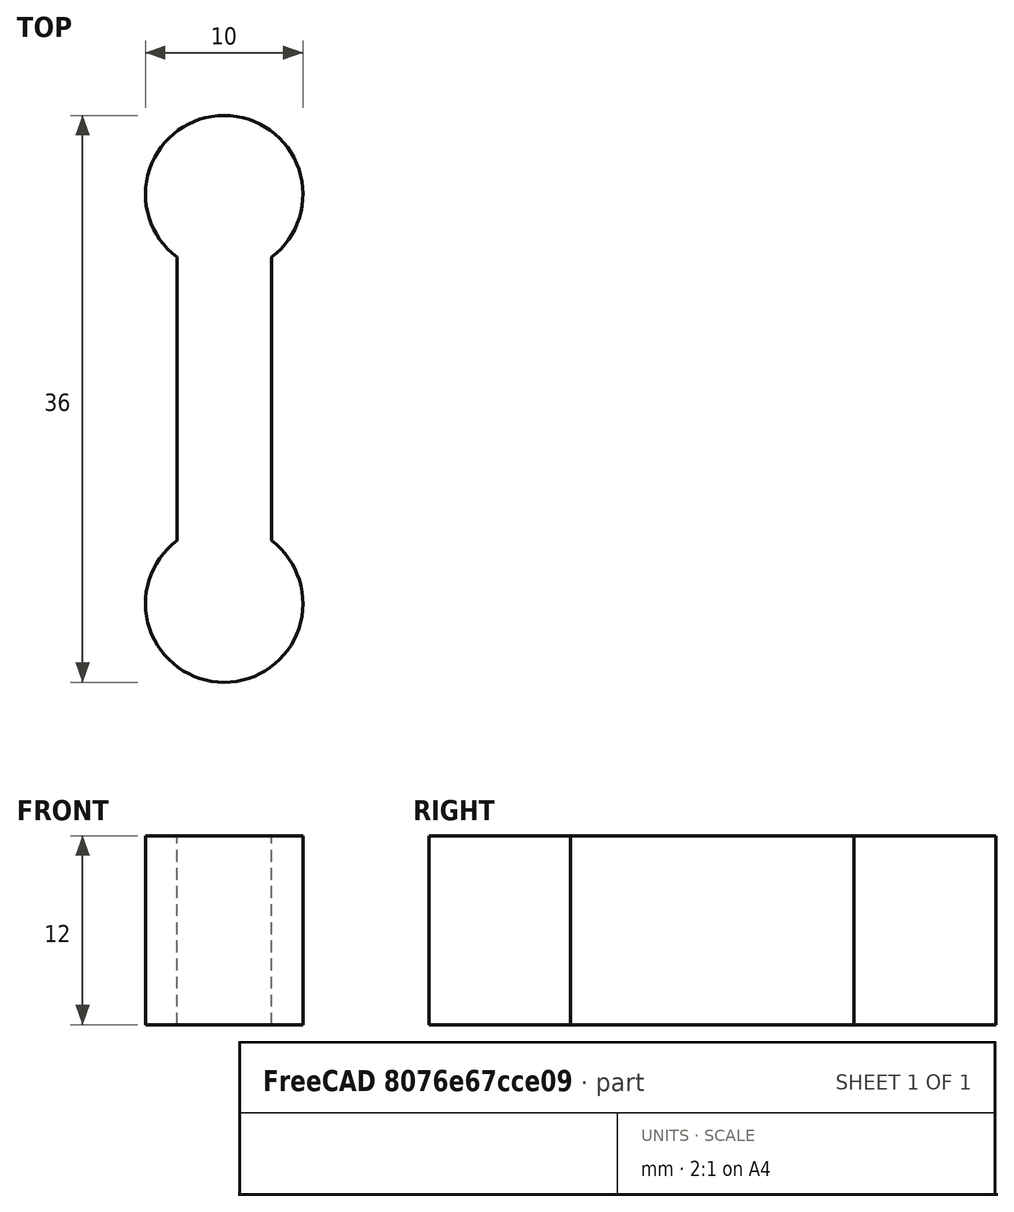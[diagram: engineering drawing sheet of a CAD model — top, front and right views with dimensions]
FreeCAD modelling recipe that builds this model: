
FCSTD DOCUMENT  (FreeCAD 0.19R24291 (Git))
Label: dog bone mk2
License: All rights reserved
LicenseURL: http://en.wikipedia.org/wiki/All_rights_reserved
objects: Sketcher::SketchObject×1, PartDesign::Pad×1, PartDesign::Body×1
note: 4 computed .brp shape members not serialized (recipe doc carries the construction recipe); baked Part::Feature solids carry a one-line shape summary decoded from their .brp

FEATURE [Sketcher::SketchObject] Sketch
  FullyConstrained = true
  MapMode = 5
  Support = -> [XY_Plane]
  sketch-geometry (8):
    g0: LineSegment StartX=-3 StartY=0 StartZ=0 EndX=0 EndY=0 EndZ=0
    g1: LineSegment StartX=0 StartY=0 StartZ=0 EndX=3 EndY=0 EndZ=0
    g2: LineSegment StartX=-3 StartY=0 StartZ=0 EndX=-3 EndY=-9 EndZ=0
    g3: LineSegment StartX=3 StartY=0 StartZ=0 EndX=3 EndY=-9 EndZ=0
    g4: LineSegment StartX=-3 StartY=0 StartZ=0 EndX=-3 EndY=9 EndZ=0
    g5: LineSegment StartX=3 StartY=0 StartZ=0 EndX=3 EndY=9 EndZ=0
    g6: ArcOfCircle CenterX=-1e-15 CenterY=13 CenterZ=0 NormalX=0 NormalY=0 NormalZ=1 AngleXU=0 Radius=5 StartAngle=5.35589 EndAngle=10.3521
    g7: ArcOfCircle CenterX=1e-15 CenterY=-13 CenterZ=0 NormalX=0 NormalY=0 NormalZ=1 AngleXU=0 Radius=5 StartAngle=2.2143 EndAngle=7.21048
  constraints (24):
    c: PointOnObject(g0,g-1)
    c: Coincident(g0,g-1)
    c: Coincident(g1,g-1)
    c: PointOnObject(g1,g-1)
    c: Equal(g0,g1)
    c: DistanceX(g0,g1) = 6
    c: Coincident(g2,g0)
    c: Vertical(g2)
    c: Coincident(g3,g1)
    c: Vertical(g3)
    c: Coincident(g4,g2)
    c: Vertical(g4)
    c: Coincident(g5,g3)
    c: Vertical(g5)
    c: Distance(g4) = 9
    c: Equal(g4,g5)
    c: Equal(g2,g4)
    c: Equal(g4,g3)
    c: Diameter(g6) = 10
    c: Diameter(g7) = 10
    c: Coincident(g6,g5)
    c: Coincident(g6,g4)
    c: Coincident(g7,g2)
    c: Coincident(g7,g3)
FEATURE [PartDesign::Pad] Pad
  Direction = (1,1,1)
  Length = 12
  Length2 = 100
  Profile = -> Sketch
  Type = 0
FEATURE [PartDesign::Body] Body
  Group = -> [Sketch,Pad]
  Origin = -> Origin
  Tip = -> Pad
